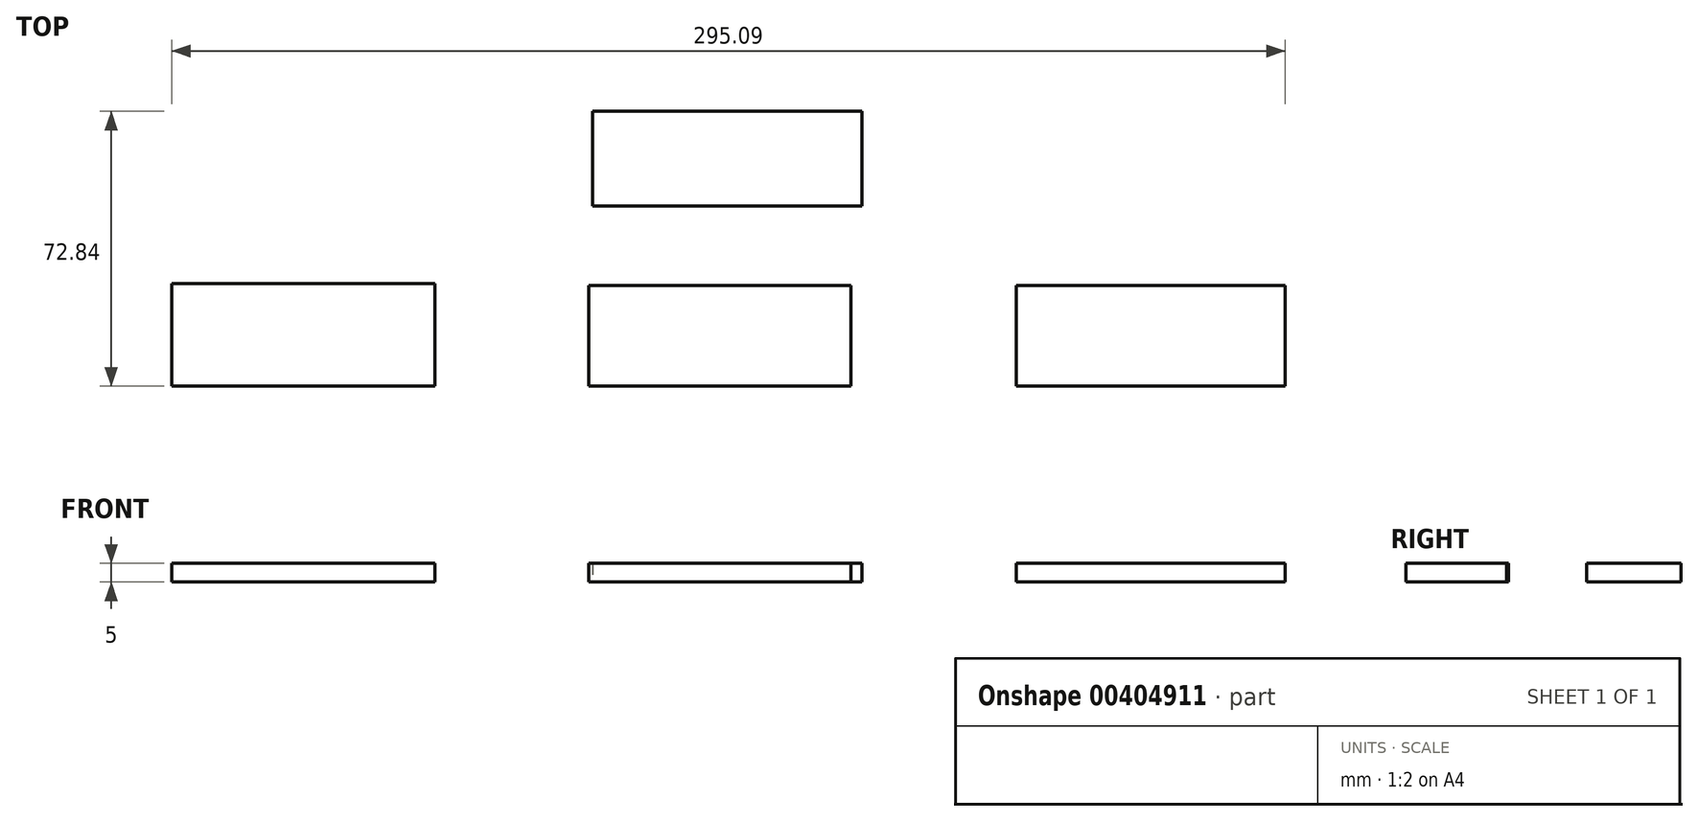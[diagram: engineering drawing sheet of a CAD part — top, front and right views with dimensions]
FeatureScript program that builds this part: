
annotation { "Feature Type Name" : "Feature", "Feature Type Description" : "" }
export const myFeature = defineFeature(function(context is Context, id is Id, definition is map)
    precondition{}
    {
        {
            var Q0;
            Q0=qCreatedBy(makeId("Top.planeOp"),FACE);
            var sketch = newSketch(context, id + "F0", { "sketchPlane" : qUnion([Q0])});
            skLineSegment(sketch, "E0.bottom", {"start": v(-30.09, 64.96) * mm, "end": v(41.27, 64.96) * mm});
            skLineSegment(sketch, "E0.top", {"start": v(-30.09, 39.92) * mm, "end": v(41.27, 39.92) * mm});
            skLineSegment(sketch, "E0.left", {"start": v(-30.09, 64.96) * mm, "end": v(-30.09, 39.92) * mm});
            skLineSegment(sketch, "E0.right", {"start": v(41.27, 64.96) * mm, "end": v(41.27, 39.92) * mm});
            skLineSegment(sketch, "E1.bottom", {"start": v(-141.62, 19.26) * mm, "end": v(-71.91, 19.26) * mm});
            skLineSegment(sketch, "E1.top", {"start": v(-141.62, -7.88) * mm, "end": v(-71.91, -7.88) * mm});
            skLineSegment(sketch, "E1.left", {"start": v(-141.62, 19.26) * mm, "end": v(-141.62, -7.88) * mm});
            skLineSegment(sketch, "E1.right", {"start": v(-71.91, 19.26) * mm, "end": v(-71.91, -7.88) * mm});
            skLineSegment(sketch, "E2.bottom", {"start": v(-31.1, 18.74) * mm, "end": v(38.31, 18.74) * mm});
            skLineSegment(sketch, "E2.top", {"start": v(-31.1, -7.88) * mm, "end": v(38.31, -7.88) * mm});
            skLineSegment(sketch, "E2.left", {"start": v(-31.1, 18.74) * mm, "end": v(-31.1, -7.88) * mm});
            skLineSegment(sketch, "E2.right", {"start": v(38.31, 18.74) * mm, "end": v(38.31, -7.88) * mm});
            skLineSegment(sketch, "E3.bottom", {"start": v(82.22, -7.88) * mm, "end": v(153.47, -7.88) * mm});
            skLineSegment(sketch, "E3.top", {"start": v(82.22, 18.74) * mm, "end": v(153.47, 18.74) * mm});
            skLineSegment(sketch, "E3.left", {"start": v(82.22, -7.88) * mm, "end": v(82.22, 18.74) * mm});
            skLineSegment(sketch, "E3.right", {"start": v(153.47, -7.88) * mm, "end": v(153.47, 18.74) * mm});
            skLineSegment(sketch, "E4", {"start": v(3.6, 39.92) * mm, "end": v(3.6, 18.74) * mm});
            skPoint(sketch, "E4.startSnap0", {"position": v(3.6, 18.74) * mm});
            skLineSegment(sketch, "E5", {"start": v(3.6, 29.33) * mm, "end": v(-106.77, 29.33) * mm});
            skPoint(sketch, "E5.endSnap0", {"position": v(-106.77, 19.26) * mm});
            skLineSegment(sketch, "E6", {"start": v(-106.77, 29.33) * mm, "end": v(-106.77, 19.26) * mm});
            skLineSegment(sketch, "E7", {"start": v(3.6, 29.33) * mm, "end": v(117.87, 29.33) * mm});
            skLineSegment(sketch, "E8", {"start": v(117.87, 29.33) * mm, "end": v(117.87, 19.26) * mm});
            skSolve(sketch);
        }
        {
            var Q0;
            Q0=makeQuery(id+"F0.imprint","IMPRINT",FACE,{"disambiguationData":[TD([[makeQuery(id+"F0.imprint","IMPRINT",EDGE,{"derivedFrom":sQuery(id+"F0.wireOp",EDGE,"E1.top")}),1.0]])]});
            var Q1;
            Q1=makeQuery(id+"F0.imprint","IMPRINT",FACE,{"disambiguationData":[TD([[makeQuery(id+"F0.imprint","IMPRINT",EDGE,{"derivedFrom":sQuery(id+"F0.wireOp",EDGE,"E0.bottom")}),-1.0]])]});
            var Q2;
            Q2=makeQuery(id+"F0.imprint","IMPRINT",FACE,{"disambiguationData":[TD([[makeQuery(id+"F0.imprint","IMPRINT",EDGE,{"derivedFrom":sQuery(id+"F0.wireOp",EDGE,"E2.top")}),1.0]])]});
            var Q3;
            Q3=makeQuery(id+"F0.imprint","IMPRINT",FACE,{"disambiguationData":[TD([[makeQuery(id+"F0.imprint","IMPRINT",EDGE,{"derivedFrom":sQuery(id+"F0.wireOp",EDGE,"E3.bottom")}),1.0]])]});
            extrude(context, id + "F1", {"entities" : qUnion([Q0, Q1, Q2, Q3]), "depth" : 5 * mm});
        }
    });
